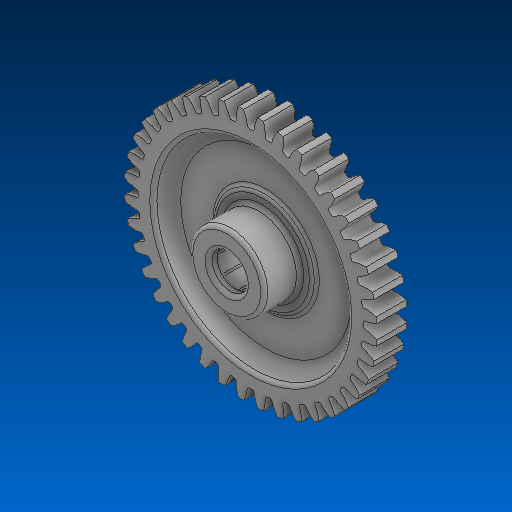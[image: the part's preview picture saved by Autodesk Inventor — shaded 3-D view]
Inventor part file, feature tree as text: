
AUTODESK INVENTOR PART (.ipt)
format: ipt  version: 2022.2 (Build 262287000, 287)  size: 626,688 bytes
history: native  units: in
note: dims shown in document units (in); Inventor stores cm internally (conversion verified against a paired STEP export)
features: fillet x1
ambient origin geometry x8: Origin, YZ Plane, XZ Plane, XY Plane, X Axis, Y Axis, Z Axis, Center Point
bodies: Solid1 (feature_tree)
feature tree (1):
  fillet  "Fillet4"  [1 undecoded]
note: 1 required parameter value undecoded (feature->parameter linkage not recoverable at this tier; creation-order binding heuristic only, values carry confidence <= 0.55)
